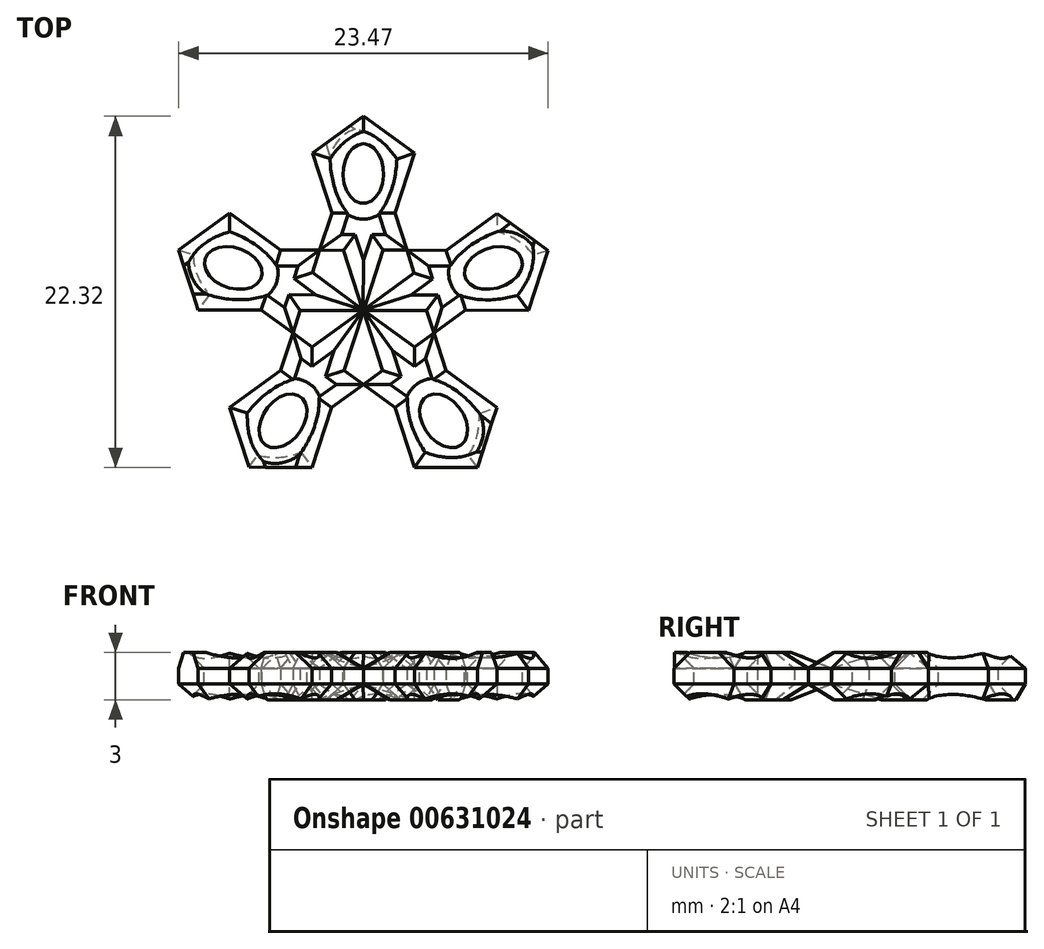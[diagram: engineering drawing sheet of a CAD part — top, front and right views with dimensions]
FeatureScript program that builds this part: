
annotation { "Feature Type Name" : "Feature", "Feature Type Description" : "" }
export const myFeature = defineFeature(function(context is Context, id is Id, definition is map)
    precondition{}
    {
        {
            var Q0;
            Q0=qCreatedBy(makeId("Top.planeOp"),FACE);
            var sketch = newSketch(context, id + "F0", { "sketchPlane" : qUnion([Q0])});
            skCircle(sketch, "E0.cCircle", {"center": v(0, 3.43) * mm, "radius": 2.75 * mm, "construction": true});
            skLineSegment(sketch, "E0.0", {"start": v(-2, 6.18) * mm, "end": v(2, 6.17) * mm});
            skLineSegment(sketch, "E0.1", {"start": v(2, 6.17) * mm, "end": v(3.23, 2.37) * mm});
            skLineSegment(sketch, "E0.2", {"start": v(3.23, 2.37) * mm, "end": v(0, 0.02) * mm});
            skLineSegment(sketch, "E0.3", {"start": v(0, 0.02) * mm, "end": v(-3.24, 2.38) * mm});
            skLineSegment(sketch, "E0.4", {"start": v(-3.24, 2.38) * mm, "end": v(-2, 6.18) * mm});
            skPoint(sketch, "E0.0.midPoint", {"position": v(0, 6.18) * mm});
            skLineSegment(sketch, "E1.MirrorCS", {"start": v(-3.22, 9.99) * mm, "end": v(-2, 6.18) * mm});
            skLineSegment(sketch, "E2.MirrorCS", {"start": v(0.02, 12.33) * mm, "end": v(-3.22, 9.99) * mm});
            skLineSegment(sketch, "E3.MirrorCS", {"start": v(3.25, 9.98) * mm, "end": v(0.02, 12.33) * mm});
            skLineSegment(sketch, "E4.MirrorCS", {"start": v(2, 6.17) * mm, "end": v(3.25, 9.98) * mm});
            skLineSegment(sketch, "E5.1.0", {"start": v(-6.5, 0.01) * mm, "end": v(-5.25, 3.82) * mm});
            skCircle(sketch, "E5.1.1", {"center": v(-3.26, 1.06) * mm, "radius": 2.75 * mm, "construction": true});
            skLineSegment(sketch, "E5.1.2", {"start": v(-5.25, 3.82) * mm, "end": v(-8.48, 6.17) * mm});
            skLineSegment(sketch, "E5.1.3", {"start": v(-11.73, 3.83) * mm, "end": v(-10.5, 0.02) * mm});
            skLineSegment(sketch, "E5.1.4", {"start": v(-3.26, -2.34) * mm, "end": v(-6.5, 0.01) * mm});
            skLineSegment(sketch, "E5.1.5", {"start": v(-0.02, 0) * mm, "end": v(-3.26, -2.34) * mm});
            skLineSegment(sketch, "E5.1.6", {"start": v(-8.48, 6.17) * mm, "end": v(-11.73, 3.83) * mm});
            skLineSegment(sketch, "E5.1.7", {"start": v(-11.73, 3.83) * mm, "end": v(-10.5, 0.02) * mm});
            skLineSegment(sketch, "E5.1.8", {"start": v(-1.25, 3.8) * mm, "end": v(-0.02, 0) * mm});
            skPoint(sketch, "E5.1.9", {"position": v(-5.87, 1.91) * mm});
            skLineSegment(sketch, "E5.1.10", {"start": v(-5.25, 3.82) * mm, "end": v(-1.25, 3.8) * mm});
            skLineSegment(sketch, "E5.1.11", {"start": v(-10.5, 0.02) * mm, "end": v(-6.5, 0.01) * mm});
            skLineSegment(sketch, "E5.2.0", {"start": v(-2.02, -6.17) * mm, "end": v(-5.25, -3.82) * mm});
            skCircle(sketch, "E5.2.1", {"center": v(-2.01, -2.77) * mm, "radius": 2.75 * mm, "construction": true});
            skLineSegment(sketch, "E5.2.2", {"start": v(-5.25, -3.82) * mm, "end": v(-8.5, -6.16) * mm});
            skLineSegment(sketch, "E5.2.3", {"start": v(-7.26, -9.97) * mm, "end": v(-3.26, -9.98) * mm});
            skLineSegment(sketch, "E5.2.4", {"start": v(1.22, -3.83) * mm, "end": v(-2.02, -6.17) * mm});
            skLineSegment(sketch, "E5.2.5", {"start": v(0, -0.02) * mm, "end": v(1.22, -3.83) * mm});
            skLineSegment(sketch, "E5.2.6", {"start": v(-8.5, -6.16) * mm, "end": v(-7.26, -9.97) * mm});
            skLineSegment(sketch, "E5.2.7", {"start": v(-7.26, -9.97) * mm, "end": v(-3.26, -9.98) * mm});
            skLineSegment(sketch, "E5.2.8", {"start": v(-4, -0.02) * mm, "end": v(0, -0.02) * mm});
            skPoint(sketch, "E5.2.9", {"position": v(-3.64, -5) * mm});
            skLineSegment(sketch, "E5.2.10", {"start": v(-5.25, -3.82) * mm, "end": v(-4, -0.02) * mm});
            skLineSegment(sketch, "E5.2.11", {"start": v(-3.26, -9.98) * mm, "end": v(-2.02, -6.17) * mm});
            skLineSegment(sketch, "E5.3.0", {"start": v(5.25, -3.83) * mm, "end": v(2, -6.17) * mm});
            skCircle(sketch, "E5.3.1", {"center": v(2.01, -2.77) * mm, "radius": 2.75 * mm, "construction": true});
            skLineSegment(sketch, "E5.3.2", {"start": v(2, -6.17) * mm, "end": v(3.24, -9.98) * mm});
            skLineSegment(sketch, "E5.3.3", {"start": v(7.24, -9.99) * mm, "end": v(8.48, -6.19) * mm});
            skLineSegment(sketch, "E5.3.4", {"start": v(4.02, -0.02) * mm, "end": v(5.25, -3.83) * mm});
            skLineSegment(sketch, "E5.3.5", {"start": v(0.02, -0.02) * mm, "end": v(4.02, -0.02) * mm});
            skLineSegment(sketch, "E5.3.6", {"start": v(3.24, -9.98) * mm, "end": v(7.24, -9.99) * mm});
            skLineSegment(sketch, "E5.3.7", {"start": v(7.24, -9.99) * mm, "end": v(8.48, -6.19) * mm});
            skLineSegment(sketch, "E5.3.8", {"start": v(-1.22, -3.82) * mm, "end": v(0.02, -0.02) * mm});
            skPoint(sketch, "E5.3.9", {"position": v(3.63, -5) * mm});
            skLineSegment(sketch, "E5.3.10", {"start": v(2, -6.17) * mm, "end": v(-1.22, -3.82) * mm});
            skLineSegment(sketch, "E5.3.11", {"start": v(8.48, -6.19) * mm, "end": v(5.25, -3.83) * mm});
            skLineSegment(sketch, "E5.4.0", {"start": v(5.26, 3.8) * mm, "end": v(6.5, 0) * mm});
            skCircle(sketch, "E5.4.1", {"center": v(3.26, 1.06) * mm, "radius": 2.75 * mm, "construction": true});
            skLineSegment(sketch, "E5.4.2", {"start": v(6.5, 0) * mm, "end": v(10.5, 0) * mm});
            skLineSegment(sketch, "E5.4.3", {"start": v(11.74, 3.8) * mm, "end": v(8.5, 6.15) * mm});
            skLineSegment(sketch, "E5.4.4", {"start": v(1.26, 3.82) * mm, "end": v(5.26, 3.8) * mm});
            skLineSegment(sketch, "E5.4.5", {"start": v(0.02, 0.01) * mm, "end": v(1.26, 3.82) * mm});
            skLineSegment(sketch, "E5.4.6", {"start": v(10.5, 0) * mm, "end": v(11.74, 3.8) * mm});
            skLineSegment(sketch, "E5.4.7", {"start": v(11.74, 3.8) * mm, "end": v(8.5, 6.15) * mm});
            skLineSegment(sketch, "E5.4.8", {"start": v(3.25, -2.34) * mm, "end": v(0.02, 0.01) * mm});
            skPoint(sketch, "E5.4.9", {"position": v(5.88, 1.9) * mm});
            skLineSegment(sketch, "E5.4.10", {"start": v(6.5, 0) * mm, "end": v(3.25, -2.34) * mm});
            skLineSegment(sketch, "E5.4.11", {"start": v(8.5, 6.15) * mm, "end": v(5.26, 3.8) * mm});
            skPoint(sketch, "E5.center", {"position": v(0, 0) * mm});
            skEllipse(sketch, "E6", {"center": v(0, 8.68) * mm, "majorRadius": 1.9 * mm, "minorRadius": 1.29 * mm, "majorAxis": v(0, 1)});
            skEllipse(sketch, "E7.1.1", {"center": v(-8.26, 2.68) * mm, "majorRadius": 1.9 * mm, "minorRadius": 1.29 * mm, "majorAxis": v(-0.95, 0.3)});
            skEllipse(sketch, "E7.2.1", {"center": v(-5.1, -7.02) * mm, "majorRadius": 1.9 * mm, "minorRadius": 1.29 * mm, "majorAxis": v(-0.59, -0.8)});
            skEllipse(sketch, "E7.3.1", {"center": v(5.1, -7.02) * mm, "majorRadius": 1.9 * mm, "minorRadius": 1.29 * mm, "majorAxis": v(0.59, -0.8)});
            skEllipse(sketch, "E7.4.1", {"center": v(8.26, 2.68) * mm, "majorRadius": 1.9 * mm, "minorRadius": 1.29 * mm, "majorAxis": v(0.95, 0.3)});
            skSolve(sketch);
        }
        {
            var Q0;
            {var subQ6=sQuery(id+"F0.wireOp",EDGE,"E0.0");Q0=makeQuery(id+"F0.imprint","IMPRINT",FACE,{"disambiguationData":[TD([[makeQuery(id+"F0.imprint","IMPRINT",EDGE,{"derivedFrom":subQ6}),-1.0]])]});}
            var Q1;
            Q1=makeQuery(id+"F0.imprint","IMPRINT",FACE,{"disambiguationData":[TD([[makeQuery(id+"F0.imprint","IMPRINT",EDGE,{"derivedFrom":sQuery(id+"F0.wireOp",EDGE,"E0.0")}),1.0]])]});
            extrude(context, id + "F1", {"entities" : qUnion([Q0, Q1]), "depth" : 3 * mm, "offsetDistance" : 25 * mm});
        }
        {
            var Q0;
            Q0=makeQuery(id+"F1.opExtrude","CAP_EDGE",EDGE,{"disambiguationData":[OSD([sQuery(id+"F0.wireOp",EDGE,"E5.1.8")])],"isStart":false});
            var Q1;
            Q1=makeQuery(id+"F1.opExtrude","CAP_EDGE",EDGE,{"disambiguationData":[OSD([sQuery(id+"F0.wireOp",EDGE,"E5.1.10")])],"isStart":false});
            var Q2;
            Q2=makeQuery(id+"F1.opExtrude","CAP_EDGE",EDGE,{"disambiguationData":[OSD([sQuery(id+"F0.wireOp",EDGE,"E0.4")])],"isStart":false});
            var Q3;
            Q3=makeQuery(id+"F1.opExtrude","CAP_EDGE",EDGE,{"disambiguationData":[OSD([sQuery(id+"F0.wireOp",EDGE,"E1.MirrorCS")])],"isStart":false});
            var Q4;
            Q4=makeQuery(id+"F1.opExtrude","CAP_EDGE",EDGE,{"disambiguationData":[OSD([sQuery(id+"F0.wireOp",EDGE,"E2.MirrorCS")])],"isStart":false});
            var Q5;
            Q5=makeQuery(id+"F1.opExtrude","CAP_EDGE",EDGE,{"disambiguationData":[OSD([sQuery(id+"F0.wireOp",EDGE,"E3.MirrorCS")])],"isStart":false});
            var Q6;
            Q6=makeQuery(id+"F1.opExtrude","CAP_EDGE",EDGE,{"disambiguationData":[OSD([sQuery(id+"F0.wireOp",EDGE,"E4.MirrorCS")])],"isStart":false});
            var Q7;
            Q7=makeQuery(id+"F1.opExtrude","CAP_EDGE",EDGE,{"disambiguationData":[OSD([sQuery(id+"F0.wireOp",EDGE,"E0.1")])],"isStart":false});
            var Q8;
            Q8=makeQuery(id+"F1.opExtrude","CAP_EDGE",EDGE,{"disambiguationData":[OSD([sQuery(id+"F0.wireOp",EDGE,"E5.4.4")])],"isStart":false});
            var Q9;
            Q9=makeQuery(id+"F1.opExtrude","CAP_FACE",FACE,{"disambiguationData":[OSD([sQuery(id+"F0.wireOp",EDGE,"E0.1"),sQuery(id+"F0.wireOp",EDGE,"E0.2"),sQuery(id+"F0.wireOp",EDGE,"E0.3"),sQuery(id+"F0.wireOp",EDGE,"E0.4"),sQuery(id+"F0.wireOp",EDGE,"E1.MirrorCS"),sQuery(id+"F0.wireOp",EDGE,"E2.MirrorCS"),sQuery(id+"F0.wireOp",EDGE,"E3.MirrorCS"),sQuery(id+"F0.wireOp",EDGE,"E4.MirrorCS"),sQuery(id+"F0.wireOp",EDGE,"E5.1.8"),sQuery(id+"F0.wireOp",EDGE,"E5.1.10"),sQuery(id+"F0.wireOp",EDGE,"E5.4.4"),sQuery(id+"F0.wireOp",EDGE,"E5.4.5"),sQuery(id+"F0.wireOp",EDGE,"E6")])],"isStart":false});
            chamfer(context, id + "F2", {"entities" : qUnion([Q0, Q1, Q2, Q3, Q4, Q5, Q6, Q7, Q8, Q9]), "width" : 1 * mm, "tangentPropagation" : true});
        }
        {
            var Q0;
            Q0=makeQuery(id+"F0.imprint","IMPRINT",FACE,{"disambiguationData":[TD([[makeQuery(id+"F0.imprint","IMPRINT",EDGE,{"derivedFrom":sQuery(id+"F0.wireOp",EDGE,"E5.4.0")}),1.0]])]});
            var Q1;
            {var subQ6=sQuery(id+"F0.wireOp",EDGE,"E5.4.0");Q1=makeQuery(id+"F0.imprint","IMPRINT",FACE,{"disambiguationData":[TD([[makeQuery(id+"F0.imprint","IMPRINT",EDGE,{"derivedFrom":subQ6}),-1.0]])]});}
            extrude(context, id + "F3", {"entities" : qUnion([Q0, Q1]), "depth" : 3 * mm, "offsetDistance" : 25 * mm});
        }
        {
            var Q0;
            Q0=makeQuery(id+"F3.opExtrude","CAP_EDGE",EDGE,{"disambiguationData":[OSD([sQuery(id+"F0.wireOp",EDGE,"E5.3.5")])],"isStart":false});
            var Q1;
            Q1=makeQuery(id+"F3.opExtrude","CAP_EDGE",EDGE,{"disambiguationData":[OSD([sQuery(id+"F0.wireOp",EDGE,"E0.2")])],"isStart":false});
            var Q2;
            Q2=makeQuery(id+"F3.opExtrude","CAP_EDGE",EDGE,{"disambiguationData":[OSD([sQuery(id+"F0.wireOp",EDGE,"E0.1")])],"isStart":false});
            var Q3;
            Q3=makeQuery(id+"F3.opExtrude","CAP_EDGE",EDGE,{"disambiguationData":[OSD([sQuery(id+"F0.wireOp",EDGE,"E5.4.4")])],"isStart":false});
            var Q4;
            Q4=makeQuery(id+"F3.opExtrude","CAP_EDGE",EDGE,{"disambiguationData":[OSD([sQuery(id+"F0.wireOp",EDGE,"E5.4.11")])],"isStart":false});
            var Q5;
            Q5=makeQuery(id+"F3.opExtrude","CAP_EDGE",EDGE,{"disambiguationData":[OSD([sQuery(id+"F0.wireOp",EDGE,"E5.4.3")])],"isStart":false});
            var Q6;
            Q6=makeQuery(id+"F3.opExtrude","CAP_EDGE",EDGE,{"disambiguationData":[OSD([sQuery(id+"F0.wireOp",EDGE,"E5.4.10")])],"isStart":false});
            var Q7;
            Q7=makeQuery(id+"F3.opExtrude","CAP_EDGE",EDGE,{"disambiguationData":[OSD([sQuery(id+"F0.wireOp",EDGE,"E5.3.4")])],"isStart":false});
            var Q8;
            Q8=makeQuery(id+"F3.opExtrude","CAP_EDGE",EDGE,{"disambiguationData":[OSD([sQuery(id+"F0.wireOp",EDGE,"E5.4.2")])],"isStart":false});
            var Q9;
            Q9=makeQuery(id+"F3.opExtrude","CAP_EDGE",EDGE,{"disambiguationData":[OSD([sQuery(id+"F0.wireOp",EDGE,"E5.4.6")])],"isStart":false});
            var Q10;
            Q10=makeQuery(id+"F3.opExtrude","CAP_EDGE",EDGE,{"disambiguationData":[OSD([sQuery(id+"F0.wireOp",EDGE,"E7.4.1")])],"isStart":false});
            chamfer(context, id + "F4", {"entities" : qUnion([Q0, Q1, Q2, Q3, Q4, Q5, Q6, Q7, Q8, Q9, Q10]), "width" : 1 * mm, "tangentPropagation" : true});
        }
        {
            var Q0;
            {var subQ1=sQuery(id+"F0.wireOp",EDGE,"E5.3.0");Q0=makeQuery(id+"F0.imprint","IMPRINT",FACE,{"disambiguationData":[TD([[makeQuery(id+"F0.imprint","IMPRINT",EDGE,{"derivedFrom":subQ1}),-1.0]])]});}
            var Q1;
            Q1=makeQuery(id+"F0.imprint","IMPRINT",FACE,{"disambiguationData":[TD([[makeQuery(id+"F0.imprint","IMPRINT",EDGE,{"derivedFrom":sQuery(id+"F0.wireOp",EDGE,"E5.3.0")}),1.0]])]});
            extrude(context, id + "F5", {"entities" : qUnion([Q0, Q1]), "depth" : 3 * mm, "offsetDistance" : 25 * mm});
        }
        {
            var Q0;
            {var subQ1=sQuery(id+"F0.wireOp",EDGE,"E5.2.0");Q0=makeQuery(id+"F0.imprint","IMPRINT",FACE,{"disambiguationData":[TD([[makeQuery(id+"F0.imprint","IMPRINT",EDGE,{"derivedFrom":subQ1}),-1.0]])]});}
            var Q1;
            Q1=makeQuery(id+"F0.imprint","IMPRINT",FACE,{"disambiguationData":[TD([[makeQuery(id+"F0.imprint","IMPRINT",EDGE,{"derivedFrom":sQuery(id+"F0.wireOp",EDGE,"E5.2.0")}),1.0]])]});
            extrude(context, id + "F6", {"entities" : qUnion([Q0, Q1]), "depth" : 3 * mm, "offsetDistance" : 25 * mm});
        }
        {
            var Q0;
            {var subQ1=sQuery(id+"F0.wireOp",EDGE,"E5.1.0");Q0=makeQuery(id+"F0.imprint","IMPRINT",FACE,{"disambiguationData":[TD([[makeQuery(id+"F0.imprint","IMPRINT",EDGE,{"derivedFrom":subQ1}),-1.0]])]});}
            var Q1;
            Q1=makeQuery(id+"F0.imprint","IMPRINT",FACE,{"disambiguationData":[TD([[makeQuery(id+"F0.imprint","IMPRINT",EDGE,{"derivedFrom":sQuery(id+"F0.wireOp",EDGE,"E5.1.0")}),1.0]])]});
            extrude(context, id + "F7", {"entities" : qUnion([Q0, Q1]), "depth" : 3 * mm, "offsetDistance" : 25 * mm});
        }
        {
            var Q0;
            Q0=makeQuery(id+"F5.opExtrude","CAP_EDGE",EDGE,{"disambiguationData":[OSD([sQuery(id+"F0.wireOp",EDGE,"E5.4.8")])],"isStart":false});
            var Q1;
            Q1=makeQuery(id+"F5.opExtrude","CAP_EDGE",EDGE,{"disambiguationData":[OSD([sQuery(id+"F0.wireOp",EDGE,"E5.4.10")])],"isStart":false});
            var Q2;
            Q2=makeQuery(id+"F5.opExtrude","CAP_EDGE",EDGE,{"disambiguationData":[OSD([sQuery(id+"F0.wireOp",EDGE,"E5.3.4")])],"isStart":false});
            var Q3;
            Q3=makeQuery(id+"F5.opExtrude","CAP_EDGE",EDGE,{"disambiguationData":[OSD([sQuery(id+"F0.wireOp",EDGE,"E5.3.11")])],"isStart":false});
            var Q4;
            Q4=makeQuery(id+"F5.opExtrude","CAP_EDGE",EDGE,{"disambiguationData":[OSD([sQuery(id+"F0.wireOp",EDGE,"E5.3.7")])],"isStart":false});
            var Q5;
            Q5=makeQuery(id+"F5.opExtrude","CAP_EDGE",EDGE,{"disambiguationData":[OSD([sQuery(id+"F0.wireOp",EDGE,"E5.3.6")])],"isStart":false});
            var Q6;
            Q6=makeQuery(id+"F5.opExtrude","CAP_EDGE",EDGE,{"disambiguationData":[OSD([sQuery(id+"F0.wireOp",EDGE,"E5.3.2")])],"isStart":false});
            var Q7;
            Q7=makeQuery(id+"F5.opExtrude","CAP_EDGE",EDGE,{"disambiguationData":[OSD([sQuery(id+"F0.wireOp",EDGE,"E5.3.10")])],"isStart":false});
            var Q8;
            Q8=makeQuery(id+"F5.opExtrude","CAP_EDGE",EDGE,{"disambiguationData":[OSD([sQuery(id+"F0.wireOp",EDGE,"E5.2.4")])],"isStart":false});
            var Q9;
            Q9=makeQuery(id+"F5.opExtrude","CAP_EDGE",EDGE,{"disambiguationData":[OSD([sQuery(id+"F0.wireOp",EDGE,"E5.2.5")])],"isStart":false});
            var Q10;
            Q10=makeQuery(id+"F5.opExtrude","CAP_EDGE",EDGE,{"disambiguationData":[OSD([sQuery(id+"F0.wireOp",EDGE,"E7.3.1")])],"isStart":false});
            chamfer(context, id + "F8", {"entities" : qUnion([Q0, Q1, Q2, Q3, Q4, Q5, Q6, Q7, Q8, Q9, Q10]), "width" : 1 * mm, "tangentPropagation" : true});
        }
        {
            var Q0;
            Q0=makeQuery(id+"F6.opExtrude","CAP_EDGE",EDGE,{"disambiguationData":[OSD([sQuery(id+"F0.wireOp",EDGE,"E7.2.1")])],"isStart":false});
            var Q1;
            Q1=makeQuery(id+"F6.opExtrude","CAP_EDGE",EDGE,{"disambiguationData":[OSD([sQuery(id+"F0.wireOp",EDGE,"E5.2.3")])],"isStart":false});
            var Q2;
            Q2=makeQuery(id+"F6.opExtrude","CAP_EDGE",EDGE,{"disambiguationData":[OSD([sQuery(id+"F0.wireOp",EDGE,"E5.2.6")])],"isStart":false});
            var Q3;
            Q3=makeQuery(id+"F6.opExtrude","CAP_EDGE",EDGE,{"disambiguationData":[OSD([sQuery(id+"F0.wireOp",EDGE,"E5.2.2")])],"isStart":false});
            var Q4;
            Q4=makeQuery(id+"F6.opExtrude","CAP_EDGE",EDGE,{"disambiguationData":[OSD([sQuery(id+"F0.wireOp",EDGE,"E5.2.10")])],"isStart":false});
            var Q5;
            Q5=makeQuery(id+"F6.opExtrude","CAP_EDGE",EDGE,{"disambiguationData":[OSD([sQuery(id+"F0.wireOp",EDGE,"E5.1.4")])],"isStart":false});
            var Q6;
            Q6=makeQuery(id+"F6.opExtrude","CAP_EDGE",EDGE,{"disambiguationData":[OSD([sQuery(id+"F0.wireOp",EDGE,"E5.1.5")])],"isStart":false});
            var Q7;
            Q7=makeQuery(id+"F6.opExtrude","CAP_EDGE",EDGE,{"disambiguationData":[OSD([sQuery(id+"F0.wireOp",EDGE,"E5.3.8")])],"isStart":false});
            var Q8;
            Q8=makeQuery(id+"F6.opExtrude","CAP_EDGE",EDGE,{"disambiguationData":[OSD([sQuery(id+"F0.wireOp",EDGE,"E5.3.10")])],"isStart":false});
            var Q9;
            Q9=makeQuery(id+"F6.opExtrude","CAP_EDGE",EDGE,{"disambiguationData":[OSD([sQuery(id+"F0.wireOp",EDGE,"E5.2.4")])],"isStart":false});
            var Q10;
            Q10=makeQuery(id+"F6.opExtrude","CAP_EDGE",EDGE,{"disambiguationData":[OSD([sQuery(id+"F0.wireOp",EDGE,"E5.2.11")])],"isStart":false});
            chamfer(context, id + "F9", {"entities" : qUnion([Q0, Q1, Q2, Q3, Q4, Q5, Q6, Q7, Q8, Q9, Q10]), "width" : 1 * mm, "tangentPropagation" : true});
        }
        {
            var Q0;
            Q0=makeQuery(id+"F7.opExtrude","CAP_EDGE",EDGE,{"disambiguationData":[OSD([sQuery(id+"F0.wireOp",EDGE,"E5.1.4")])],"isStart":false});
            var Q1;
            Q1=makeQuery(id+"F7.opExtrude","CAP_EDGE",EDGE,{"disambiguationData":[OSD([sQuery(id+"F0.wireOp",EDGE,"E5.2.10")])],"isStart":false});
            var Q2;
            Q2=makeQuery(id+"F7.opExtrude","CAP_EDGE",EDGE,{"disambiguationData":[OSD([sQuery(id+"F0.wireOp",EDGE,"E5.2.8")])],"isStart":false});
            var Q3;
            Q3=makeQuery(id+"F7.opExtrude","CAP_EDGE",EDGE,{"disambiguationData":[OSD([sQuery(id+"F0.wireOp",EDGE,"E0.3")])],"isStart":false});
            var Q4;
            Q4=makeQuery(id+"F7.opExtrude","CAP_EDGE",EDGE,{"disambiguationData":[OSD([sQuery(id+"F0.wireOp",EDGE,"E0.4")])],"isStart":false});
            var Q5;
            Q5=makeQuery(id+"F7.opExtrude","CAP_EDGE",EDGE,{"disambiguationData":[OSD([sQuery(id+"F0.wireOp",EDGE,"E5.1.10")])],"isStart":false});
            var Q6;
            Q6=makeQuery(id+"F7.opExtrude","CAP_EDGE",EDGE,{"disambiguationData":[OSD([sQuery(id+"F0.wireOp",EDGE,"E5.1.2")])],"isStart":false});
            var Q7;
            Q7=makeQuery(id+"F7.opExtrude","CAP_EDGE",EDGE,{"disambiguationData":[OSD([sQuery(id+"F0.wireOp",EDGE,"E5.1.6")])],"isStart":false});
            var Q8;
            Q8=makeQuery(id+"F7.opExtrude","CAP_EDGE",EDGE,{"disambiguationData":[OSD([sQuery(id+"F0.wireOp",EDGE,"E5.1.3")])],"isStart":false});
            var Q9;
            Q9=makeQuery(id+"F7.opExtrude","CAP_EDGE",EDGE,{"disambiguationData":[OSD([sQuery(id+"F0.wireOp",EDGE,"E5.1.11")])],"isStart":false});
            var Q10;
            Q10=makeQuery(id+"F7.opExtrude","CAP_EDGE",EDGE,{"disambiguationData":[OSD([sQuery(id+"F0.wireOp",EDGE,"E7.1.1")])],"isStart":false});
            chamfer(context, id + "F10", {"entities" : qUnion([Q0, Q1, Q2, Q3, Q4, Q5, Q6, Q7, Q8, Q9, Q10]), "width" : 1 * mm, "tangentPropagation" : true});
        }
        {
            var Q0;
            Q0=makeQuery(id+"F1.opExtrude","CAP_EDGE",EDGE,{"disambiguationData":[OSD([sQuery(id+"F0.wireOp",EDGE,"E2.MirrorCS")])],"isStart":true});
            var Q1;
            Q1=makeQuery(id+"F1.opExtrude","CAP_EDGE",EDGE,{"disambiguationData":[OSD([sQuery(id+"F0.wireOp",EDGE,"E3.MirrorCS")])],"isStart":true});
            var Q2;
            Q2=makeQuery(id+"F1.opExtrude","CAP_EDGE",EDGE,{"disambiguationData":[OSD([sQuery(id+"F0.wireOp",EDGE,"E4.MirrorCS")])],"isStart":true});
            var Q3;
            Q3=makeQuery(id+"F1.opExtrude","CAP_EDGE",EDGE,{"disambiguationData":[OSD([sQuery(id+"F0.wireOp",EDGE,"E0.1")])],"isStart":true});
            var Q4;
            Q4=makeQuery(id+"F1.opExtrude","CAP_EDGE",EDGE,{"disambiguationData":[OSD([sQuery(id+"F0.wireOp",EDGE,"E5.4.4")])],"isStart":true});
            var Q5;
            Q5=makeQuery(id+"F1.opExtrude","CAP_EDGE",EDGE,{"disambiguationData":[OSD([sQuery(id+"F0.wireOp",EDGE,"E5.4.5")])],"isStart":true});
            var Q6;
            Q6=makeQuery(id+"F1.opExtrude","CAP_EDGE",EDGE,{"disambiguationData":[OSD([sQuery(id+"F0.wireOp",EDGE,"E5.1.8")])],"isStart":true});
            var Q7;
            Q7=makeQuery(id+"F1.opExtrude","CAP_EDGE",EDGE,{"disambiguationData":[OSD([sQuery(id+"F0.wireOp",EDGE,"E5.1.10")])],"isStart":true});
            var Q8;
            Q8=makeQuery(id+"F1.opExtrude","CAP_EDGE",EDGE,{"disambiguationData":[OSD([sQuery(id+"F0.wireOp",EDGE,"E0.4")])],"isStart":true});
            var Q9;
            Q9=makeQuery(id+"F1.opExtrude","CAP_EDGE",EDGE,{"disambiguationData":[OSD([sQuery(id+"F0.wireOp",EDGE,"E1.MirrorCS")])],"isStart":true});
            var Q10;
            Q10=makeQuery(id+"F1.opExtrude","CAP_EDGE",EDGE,{"disambiguationData":[OSD([sQuery(id+"F0.wireOp",EDGE,"E6")])],"isStart":true});
            chamfer(context, id + "F11", {"entities" : qUnion([Q0, Q1, Q2, Q3, Q4, Q5, Q6, Q7, Q8, Q9, Q10]), "width" : 1 * mm, "tangentPropagation" : true});
        }
        {
            var Q0;
            Q0=makeQuery(id+"F3.opExtrude","CAP_FACE",FACE,{"disambiguationData":[OSD([sQuery(id+"F0.wireOp",EDGE,"E0.1"),sQuery(id+"F0.wireOp",EDGE,"E0.2"),sQuery(id+"F0.wireOp",EDGE,"E5.3.4"),sQuery(id+"F0.wireOp",EDGE,"E5.3.5"),sQuery(id+"F0.wireOp",EDGE,"E5.4.2"),sQuery(id+"F0.wireOp",EDGE,"E5.4.4"),sQuery(id+"F0.wireOp",EDGE,"E5.4.5"),sQuery(id+"F0.wireOp",EDGE,"E5.4.6"),sQuery(id+"F0.wireOp",EDGE,"E5.4.8"),sQuery(id+"F0.wireOp",EDGE,"E5.4.10"),sQuery(id+"F0.wireOp",EDGE,"E5.4.11"),sQuery(id+"F0.wireOp",EDGE,"E5.4.3"),sQuery(id+"F0.wireOp",EDGE,"E7.4.1")])],"isStart":true});
            chamfer(context, id + "F12", {"entities" : qUnion([Q0]), "width" : 1 * mm, "tangentPropagation" : true});
        }
        {
            var Q0;
            Q0=makeQuery(id+"F5.opExtrude","CAP_FACE",FACE,{"disambiguationData":[OSD([sQuery(id+"F0.wireOp",EDGE,"E5.2.4"),sQuery(id+"F0.wireOp",EDGE,"E5.2.5"),sQuery(id+"F0.wireOp",EDGE,"E5.3.2"),sQuery(id+"F0.wireOp",EDGE,"E5.3.4"),sQuery(id+"F0.wireOp",EDGE,"E5.3.5"),sQuery(id+"F0.wireOp",EDGE,"E5.3.6"),sQuery(id+"F0.wireOp",EDGE,"E5.3.7"),sQuery(id+"F0.wireOp",EDGE,"E5.3.8"),sQuery(id+"F0.wireOp",EDGE,"E5.3.10"),sQuery(id+"F0.wireOp",EDGE,"E5.3.11"),sQuery(id+"F0.wireOp",EDGE,"E5.4.8"),sQuery(id+"F0.wireOp",EDGE,"E5.4.10"),sQuery(id+"F0.wireOp",EDGE,"E7.3.1")])],"isStart":true});
            chamfer(context, id + "F13", {"entities" : qUnion([Q0]), "width" : 1 * mm, "tangentPropagation" : true});
        }
        {
            var Q0;
            Q0=makeQuery(id+"F6.opExtrude","CAP_FACE",FACE,{"disambiguationData":[OSD([sQuery(id+"F0.wireOp",EDGE,"E5.1.4"),sQuery(id+"F0.wireOp",EDGE,"E5.1.5"),sQuery(id+"F0.wireOp",EDGE,"E5.2.2"),sQuery(id+"F0.wireOp",EDGE,"E5.2.4"),sQuery(id+"F0.wireOp",EDGE,"E5.2.5"),sQuery(id+"F0.wireOp",EDGE,"E5.2.6"),sQuery(id+"F0.wireOp",EDGE,"E5.2.8"),sQuery(id+"F0.wireOp",EDGE,"E5.2.10"),sQuery(id+"F0.wireOp",EDGE,"E5.2.11"),sQuery(id+"F0.wireOp",EDGE,"E5.3.8"),sQuery(id+"F0.wireOp",EDGE,"E5.3.10"),sQuery(id+"F0.wireOp",EDGE,"E7.2.1"),sQuery(id+"F0.wireOp",EDGE,"E5.2.3")])],"isStart":true});
            chamfer(context, id + "F14", {"entities" : qUnion([Q0]), "width" : 1 * mm, "tangentPropagation" : true});
        }
        {
            var Q0;
            Q0=makeQuery(id+"F7.opExtrude","CAP_FACE",FACE,{"disambiguationData":[OSD([sQuery(id+"F0.wireOp",EDGE,"E0.3"),sQuery(id+"F0.wireOp",EDGE,"E0.4"),sQuery(id+"F0.wireOp",EDGE,"E5.1.2"),sQuery(id+"F0.wireOp",EDGE,"E5.1.4"),sQuery(id+"F0.wireOp",EDGE,"E5.1.5"),sQuery(id+"F0.wireOp",EDGE,"E5.1.6"),sQuery(id+"F0.wireOp",EDGE,"E5.1.8"),sQuery(id+"F0.wireOp",EDGE,"E5.1.10"),sQuery(id+"F0.wireOp",EDGE,"E5.1.11"),sQuery(id+"F0.wireOp",EDGE,"E5.2.8"),sQuery(id+"F0.wireOp",EDGE,"E5.2.10"),sQuery(id+"F0.wireOp",EDGE,"E7.1.1"),sQuery(id+"F0.wireOp",EDGE,"E5.1.3")])],"isStart":true});
            chamfer(context, id + "F15", {"entities" : qUnion([Q0]), "width" : 1 * mm, "tangentPropagation" : true});
        }
    });
